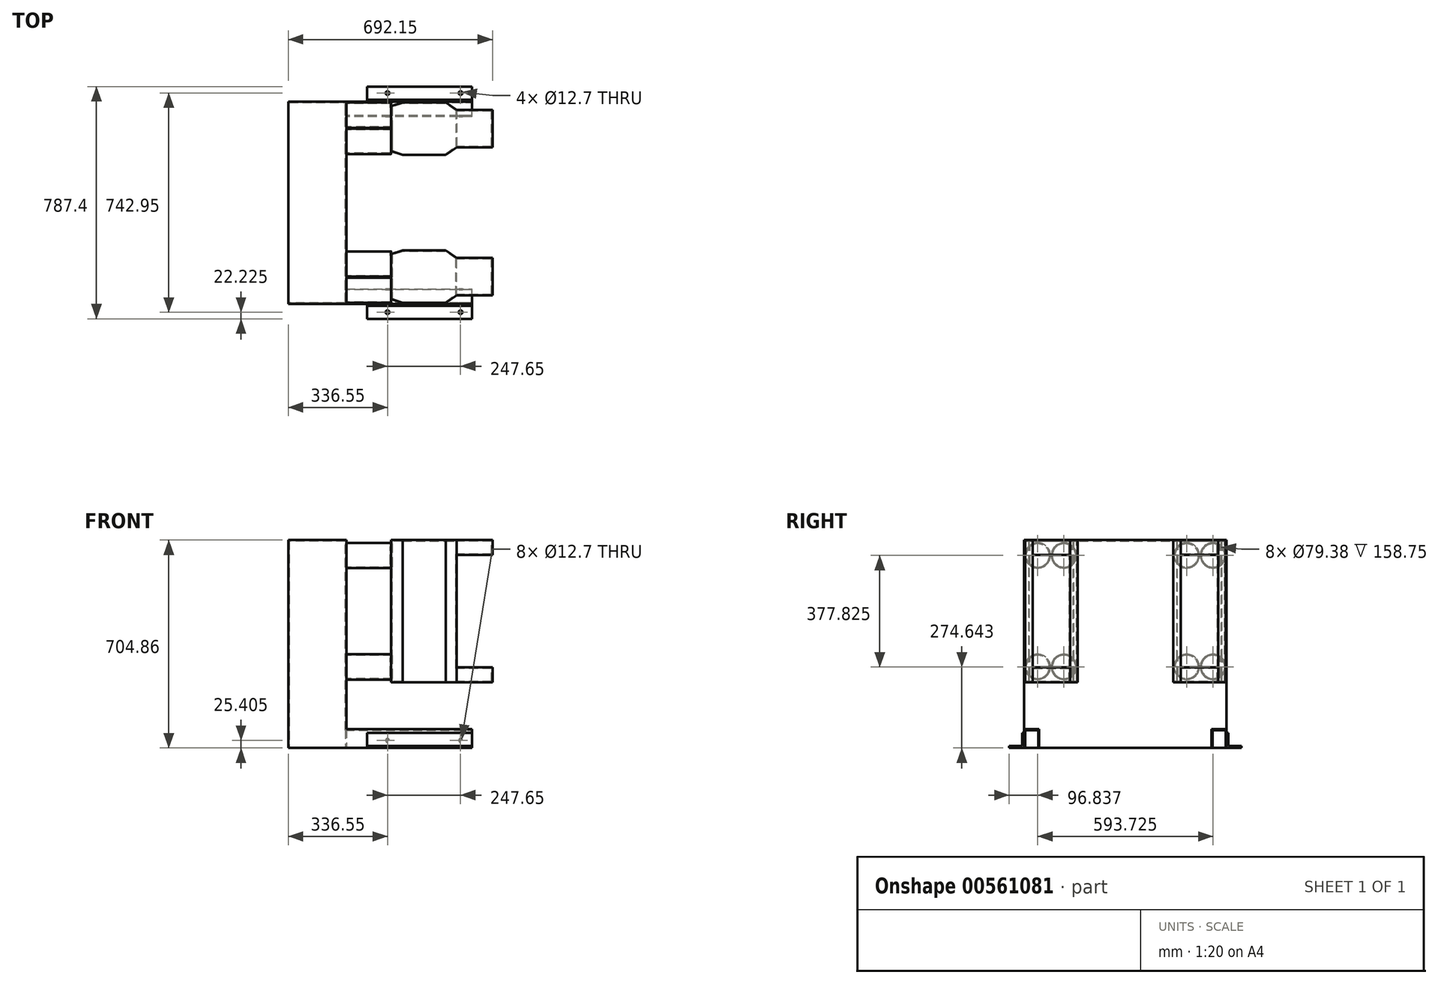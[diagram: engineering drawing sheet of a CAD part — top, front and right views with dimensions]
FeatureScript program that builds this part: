
annotation { "Feature Type Name" : "Feature", "Feature Type Description" : "" }
export const myFeature = defineFeature(function(context is Context, id is Id, definition is map)
    precondition{}
    {
        {
            var Q0;
            Q0=qCreatedBy(makeId("Front.planeOp"),FACE);
            var sketch = newSketch(context, id + "F0", { "sketchPlane" : qUnion([Q0])});
            skLineSegment(sketch, "E0", {"start": v(-114.3, 352.43) * mm, "end": v(-311.15, 352.43) * mm});
            skLineSegment(sketch, "E1", {"start": v(-311.15, 352.43) * mm, "end": v(-311.15, -352.43) * mm});
            skLineSegment(sketch, "E2", {"start": v(-311.15, -352.43) * mm, "end": v(311.15, -352.43) * mm});
            skLineSegment(sketch, "E3", {"start": v(311.15, -352.43) * mm, "end": v(311.15, -288.93) * mm});
            skLineSegment(sketch, "E4", {"start": v(311.15, -288.92) * mm, "end": v(-114.3, -288.93) * mm});
            skLineSegment(sketch, "E5", {"start": v(-114.3, -288.93) * mm, "end": v(-114.3, 352.43) * mm});
            skSolve(sketch);
        }
        {
            var Q0;
            Q0=qSketchRegion(id+"F0",true);
            extrude(context, id + "F1", {"entities" : qUnion([Q0]), "depth" : 342.9 * mm, "offsetDistance" : 25.4 * mm, "hasSecondDirection" : true, "secondDirectionOppositeDirection" : true, "secondDirectionDepth" : 342.9 * mm});
        }
        {
            var Q0;
            Q0=makeQuery(id+"F1.opExtrude","SWEPT_FACE",FACE,{"disambiguationData":[OSD([sQuery(id+"F0.wireOp",EDGE,"E5")])]});
            var sketch = newSketch(context, id + "F2", { "sketchPlane" : qUnion([Q0])});
            skCircle(sketch, "E6", {"center": v(-296.86, 300.04) * mm, "radius": 42.86 * mm});
            skCircle(sketch, "E7", {"center": v(-207.96, 300.04) * mm, "radius": 42.86 * mm});
            skCircle(sketch, "E8", {"center": v(207.96, 300.04) * mm, "radius": 42.86 * mm});
            skCircle(sketch, "E9", {"center": v(296.86, 300.04) * mm, "radius": 42.86 * mm});
            skCircle(sketch, "E10", {"center": v(-296.86, -77.79) * mm, "radius": 42.86 * mm});
            skCircle(sketch, "E11", {"center": v(-207.96, -77.79) * mm, "radius": 42.86 * mm});
            skCircle(sketch, "E12", {"center": v(207.96, -77.79) * mm, "radius": 42.86 * mm});
            skCircle(sketch, "E13", {"center": v(296.86, -77.79) * mm, "radius": 42.86 * mm});
            skSolve(sketch);
        }
        {
            var Q0;
            Q0=qSketchRegion(id+"F2",true);
            extrude(context, id + "F3", {"entities" : qUnion([Q0]), "operationType" : NewBodyOperationType.ADD, "depth" : 152.4 * mm, "offsetDistance" : 25.4 * mm});
        }
        {
            var Q0;
            Q0=makeQuery(id+"F1.opExtrude","SWEPT_FACE",FACE,{"disambiguationData":[OSD([sQuery(id+"F0.wireOp",EDGE,"E0")])]});
            var sketch = newSketch(context, id + "F4", { "sketchPlane" : qUnion([Q0])});
            skLineSegment(sketch, "E14", {"start": v(38.1, -174.63) * mm, "end": v(38.1, -327.03) * mm});
            skLineSegment(sketch, "E15", {"start": v(38.1, -327.03) * mm, "end": v(76.2, -339.73) * mm});
            skLineSegment(sketch, "E16", {"start": v(76.2, -339.73) * mm, "end": v(222.25, -339.73) * mm});
            skLineSegment(sketch, "E17", {"start": v(222.25, -339.73) * mm, "end": v(260.35, -314.33) * mm});
            skLineSegment(sketch, "E18", {"start": v(260.35, -314.33) * mm, "end": v(260.35, -187.33) * mm});
            skLineSegment(sketch, "E19", {"start": v(260.35, -187.33) * mm, "end": v(222.25, -161.93) * mm});
            skLineSegment(sketch, "E20", {"start": v(222.25, -161.93) * mm, "end": v(76.2, -161.93) * mm});
            skLineSegment(sketch, "E21", {"start": v(76.2, -161.93) * mm, "end": v(38.1, -174.63) * mm});
            skLineSegment(sketch, "E22", {"start": v(38.1, 327.03) * mm, "end": v(38.1, 174.63) * mm});
            skLineSegment(sketch, "E23", {"start": v(38.1, 174.63) * mm, "end": v(76.2, 161.93) * mm});
            skLineSegment(sketch, "E24", {"start": v(76.2, 161.93) * mm, "end": v(222.25, 161.93) * mm});
            skLineSegment(sketch, "E25", {"start": v(222.25, 161.93) * mm, "end": v(260.35, 187.33) * mm});
            skLineSegment(sketch, "E26", {"start": v(260.35, 187.33) * mm, "end": v(260.35, 314.33) * mm});
            skLineSegment(sketch, "E27", {"start": v(260.35, 314.33) * mm, "end": v(222.25, 339.73) * mm});
            skLineSegment(sketch, "E28", {"start": v(222.25, 339.73) * mm, "end": v(76.2, 339.73) * mm});
            skLineSegment(sketch, "E29", {"start": v(76.2, 339.73) * mm, "end": v(38.1, 327.03) * mm});
            skSolve(sketch);
        }
        {
            var Q0;
            Q0=qSketchRegion(id+"F4",true);
            extrude(context, id + "F5", {"entities" : qUnion([Q0]), "operationType" : NewBodyOperationType.ADD, "oppositeDirection" : true, "depth" : 482.6 * mm, "offsetDistance" : 25.4 * mm});
        }
        {
            var Q0;
            Q0=makeQuery(id+"F5.opExtrude","SWEPT_FACE",FACE,{"disambiguationData":[OSD([sQuery(id+"F4.wireOp",EDGE,"E18")])]});
            var sketch = newSketch(context, id + "F6", { "sketchPlane" : qUnion([Q0])});
            skLineSegment(sketch, "E30.bottom", {"start": v(-314.33, 352.43) * mm, "end": v(-187.33, 352.43) * mm});
            skLineSegment(sketch, "E30.top", {"start": v(-314.33, 301.62) * mm, "end": v(-187.33, 301.62) * mm});
            skLineSegment(sketch, "E30.left", {"start": v(-314.33, 352.43) * mm, "end": v(-314.33, 301.62) * mm});
            skLineSegment(sketch, "E30.right", {"start": v(-187.33, 352.43) * mm, "end": v(-187.33, 301.62) * mm});
            skLineSegment(sketch, "E31.bottom", {"start": v(-314.33, -130.18) * mm, "end": v(-187.33, -130.18) * mm});
            skLineSegment(sketch, "E31.top", {"start": v(-314.33, -79.38) * mm, "end": v(-187.33, -79.38) * mm});
            skLineSegment(sketch, "E31.left", {"start": v(-314.33, -130.18) * mm, "end": v(-314.33, -79.38) * mm});
            skLineSegment(sketch, "E31.right", {"start": v(-187.33, -130.18) * mm, "end": v(-187.33, -79.38) * mm});
            skSolve(sketch);
        }
        {
            var Q0;
            Q0=qSketchRegion(id+"F6",true);
            extrude(context, id + "F7", {"entities" : qUnion([Q0]), "operationType" : NewBodyOperationType.ADD, "depth" : 120.65 * mm, "offsetDistance" : 25.4 * mm});
        }
        {
            var Q0;
            Q0=makeQuery(id+"F5.opExtrude","SWEPT_FACE",FACE,{"disambiguationData":[OSD([sQuery(id+"F4.wireOp",EDGE,"E26")])]});
            var sketch = newSketch(context, id + "F8", { "sketchPlane" : qUnion([Q0])});
            skLineSegment(sketch, "E32.bottom", {"start": v(314.33, 352.43) * mm, "end": v(187.33, 352.43) * mm});
            skLineSegment(sketch, "E32.top", {"start": v(314.33, 301.62) * mm, "end": v(187.33, 301.62) * mm});
            skLineSegment(sketch, "E32.left", {"start": v(314.33, 352.43) * mm, "end": v(314.33, 301.62) * mm});
            skLineSegment(sketch, "E32.right", {"start": v(187.33, 352.43) * mm, "end": v(187.33, 301.62) * mm});
            skLineSegment(sketch, "E33.bottom", {"start": v(314.33, -130.18) * mm, "end": v(187.33, -130.18) * mm});
            skLineSegment(sketch, "E33.top", {"start": v(314.33, -79.37) * mm, "end": v(187.33, -79.38) * mm});
            skLineSegment(sketch, "E33.left", {"start": v(314.33, -130.18) * mm, "end": v(314.33, -79.37) * mm});
            skLineSegment(sketch, "E33.right", {"start": v(187.33, -130.18) * mm, "end": v(187.33, -79.38) * mm});
            skSolve(sketch);
        }
        {
            var Q0;
            Q0=qSketchRegion(id+"F8",true);
            extrude(context, id + "F9", {"entities" : qUnion([Q0]), "operationType" : NewBodyOperationType.ADD, "depth" : 120.65 * mm, "offsetDistance" : 25.4 * mm});
        }
        {
            var Q0;
            Q0=makeQuery(id+"F1.opExtrude","SWEPT_FACE",FACE,{"disambiguationData":[OSD([sQuery(id+"F0.wireOp",EDGE,"E2")])]});
            var sketch = newSketch(context, id + "F10", { "sketchPlane" : qUnion([Q0])});
            skLineSegment(sketch, "E34.bottom", {"start": v(311.15, 292.1) * mm, "end": v(-114.3, 292.1) * mm});
            skLineSegment(sketch, "E34.top", {"start": v(311.15, -292.1) * mm, "end": v(-114.3, -292.1) * mm});
            skLineSegment(sketch, "E34.left", {"start": v(311.15, 292.1) * mm, "end": v(311.15, -292.1) * mm});
            skLineSegment(sketch, "E34.right", {"start": v(-114.3, 292.1) * mm, "end": v(-114.3, -292.1) * mm});
            skSolve(sketch);
        }
        {
            var Q0;
            Q0=qSketchRegion(id+"F10",true);
            var Q1;
            Q1=makeQuery(id+"F1.opExtrude","SWEPT_FACE",FACE,{"disambiguationData":[OSD([sQuery(id+"F0.wireOp",EDGE,"E4")])]});
            extrude(context, id + "F11", {"entities" : qUnion([Q0]), "operationType" : NewBodyOperationType.REMOVE, "endBound" : BoundingType.UP_TO_SURFACE, "oppositeDirection" : true, "depth" : 25.4 * mm, "endBoundEntityFace" : qUnion([Q1]), "offsetDistance" : 25.4 * mm});
        }
        {
            var Q0;
            {var subQ1=sQuery(id+"F0.wireOp",EDGE,"E3");Q0=makeQuery(id+"F11.boolean.opBoolean","SPLIT",FACE,{"disambiguationData":[TD([makeQuery(id+"F11.opExtrude","SWEPT_FACE",FACE,{"disambiguationData":[OSD([sQuery(id+"F10.wireOp",EDGE,"E34.bottom")])]})])],"derivedFrom":makeQuery(id+"F1.opExtrude","SWEPT_FACE",FACE,{"disambiguationData":[OSD([subQ1])]})});}
            var Q1;
            Q1=makeQuery(id+"F1.opExtrude","SWEPT_FACE",FACE,{"disambiguationData":[OSD([sQuery(id+"F0.wireOp",EDGE,"E2")])]});
            var Q2;
            {var subQ1=sQuery(id+"F0.wireOp",EDGE,"E3");Q2=makeQuery(id+"F11.boolean.opBoolean","SPLIT",FACE,{"disambiguationData":[TD([makeQuery(id+"F11.opExtrude","SWEPT_FACE",FACE,{"disambiguationData":[OSD([sQuery(id+"F10.wireOp",EDGE,"E34.top")])]})])],"derivedFrom":makeQuery(id+"F1.opExtrude","SWEPT_FACE",FACE,{"disambiguationData":[OSD([subQ1])]})});}
            shell(context, id + "F12", {"entities" : qUnion([Q0, Q1, Q2]), "thickness" : 3.17 * mm});
        }
        {
            var Q0;
            Q0=makeQuery(id+"F1.opExtrude","CAP_FACE",FACE,{"disambiguationData":[OSD([sQuery(id+"F0.wireOp",EDGE,"E0"),sQuery(id+"F0.wireOp",EDGE,"E1"),sQuery(id+"F0.wireOp",EDGE,"E2"),sQuery(id+"F0.wireOp",EDGE,"E3"),sQuery(id+"F0.wireOp",EDGE,"E4"),sQuery(id+"F0.wireOp",EDGE,"E5")])],"isStart":false});
            var sketch = newSketch(context, id + "F13", { "sketchPlane" : qUnion([Q0])});
            skCircle(sketch, "E35", {"center": v(25.4, -327.03) * mm, "radius": 6.35 * mm});
            skCircle(sketch, "E36", {"center": v(273.05, -327.03) * mm, "radius": 6.35 * mm});
            skSolve(sketch);
        }
        {
            var Q0;
            Q0=qSketchRegion(id+"F13",true);
            extrude(context, id + "F14", {"entities" : qUnion([Q0]), "operationType" : NewBodyOperationType.REMOVE, "endBound" : BoundingType.THROUGH_ALL, "oppositeDirection" : true, "depth" : 25.4 * mm, "offsetDistance" : 25.4 * mm});
        }
        {
            var Q0;
            {var subQ1=sQuery(id+"F0.wireOp",EDGE,"E3");Q0=makeQuery(id+"F11.boolean.opBoolean","SPLIT",FACE,{"disambiguationData":[TD([makeQuery(id+"F11.opExtrude","SWEPT_FACE",FACE,{"disambiguationData":[OSD([sQuery(id+"F10.wireOp",EDGE,"E34.bottom")])]})])],"derivedFrom":makeQuery(id+"F1.opExtrude","SWEPT_FACE",FACE,{"disambiguationData":[OSD([subQ1])]})});}
            var sketch = newSketch(context, id + "F15", { "sketchPlane" : qUnion([Q0])});
            skLineSegment(sketch, "E37", {"start": v(-342.9, -352.43) * mm, "end": v(-342.9, -301.62) * mm});
            skLineSegment(sketch, "E38", {"start": v(-342.9, -301.62) * mm, "end": v(-349.25, -301.62) * mm});
            skLineSegment(sketch, "E39", {"start": v(-349.25, -301.62) * mm, "end": v(-349.25, -346.07) * mm});
            skLineSegment(sketch, "E40", {"start": v(-349.25, -346.07) * mm, "end": v(-393.7, -346.07) * mm});
            skLineSegment(sketch, "E41", {"start": v(-393.7, -346.07) * mm, "end": v(-393.7, -352.43) * mm});
            skLineSegment(sketch, "E42", {"start": v(-393.7, -352.43) * mm, "end": v(-342.9, -352.43) * mm});
            skSolve(sketch);
        }
        {
            var Q0;
            Q0 = qSketchRegion(id + "F15", true);
            extrude(context, id + "F16", {"entities" : qUnion([Q0]), "oppositeDirection" : true, "depth" : 355.6 * mm, "offsetDistance" : 25.4 * mm});
        }
        {
            var Q0;
            {var subQ1=sQuery(id+"F0.wireOp",EDGE,"E3");Q0=makeQuery(id+"F11.boolean.opBoolean","SPLIT",FACE,{"disambiguationData":[TD([makeQuery(id+"F11.opExtrude","SWEPT_FACE",FACE,{"disambiguationData":[OSD([sQuery(id+"F10.wireOp",EDGE,"E34.top")])]})])],"derivedFrom":makeQuery(id+"F1.opExtrude","SWEPT_FACE",FACE,{"disambiguationData":[OSD([subQ1])]})});}
            var sketch = newSketch(context, id + "F17", { "sketchPlane" : qUnion([Q0])});
            skLineSegment(sketch, "E43", {"start": v(342.9, -352.43) * mm, "end": v(393.7, -352.43) * mm});
            skLineSegment(sketch, "E44", {"start": v(393.7, -352.43) * mm, "end": v(393.7, -346.07) * mm});
            skLineSegment(sketch, "E45", {"start": v(393.7, -346.07) * mm, "end": v(349.25, -346.07) * mm});
            skLineSegment(sketch, "E46", {"start": v(349.25, -346.07) * mm, "end": v(349.25, -301.62) * mm});
            skLineSegment(sketch, "E47", {"start": v(349.25, -301.62) * mm, "end": v(342.9, -301.62) * mm});
            skLineSegment(sketch, "E48", {"start": v(342.9, -301.62) * mm, "end": v(342.9, -352.43) * mm});
            skSolve(sketch);
        }
        {
            var Q0;
            Q0 = qSketchRegion(id + "F17", true);
            extrude(context, id + "F18", {"entities" : qUnion([Q0]), "oppositeDirection" : true, "depth" : 355.6 * mm, "offsetDistance" : 25.4 * mm});
        }
        {
            var Q0;
            Q0=makeQuery(id+"F18.opExtrude","SWEPT_FACE",FACE,{"disambiguationData":[OSD([sQuery(id+"F17.wireOp",EDGE,"E45")])]});
            var sketch = newSketch(context, id + "F19", { "sketchPlane" : qUnion([Q0])});
            skCircle(sketch, "E49", {"center": v(25.4, 371.48) * mm, "radius": 6.35 * mm});
            skCircle(sketch, "E50", {"center": v(273.05, 371.48) * mm, "radius": 6.35 * mm});
            skCircle(sketch, "E51", {"center": v(25.4, -371.48) * mm, "radius": 6.35 * mm});
            skCircle(sketch, "E52", {"center": v(273.05, -371.48) * mm, "radius": 6.35 * mm});
            skSolve(sketch);
        }
        {
            var Q0;
            Q0 = qSketchRegion(id + "F19", true);
            var Q1;
            Q1=makeQuery(id+"F16.opExtrude","SWEPT_FACE",FACE,{"disambiguationData":[OSD([sQuery(id+"F15.wireOp",EDGE,"E42")])]});
            extrude(context, id + "F20", {"entities" : qUnion([Q0]), "operationType" : NewBodyOperationType.REMOVE, "endBound" : BoundingType.UP_TO_SURFACE, "oppositeDirection" : true, "depth" : 25.4 * mm, "endBoundEntityFace" : qUnion([Q1]), "offsetDistance" : 25.4 * mm});
        }
    });
